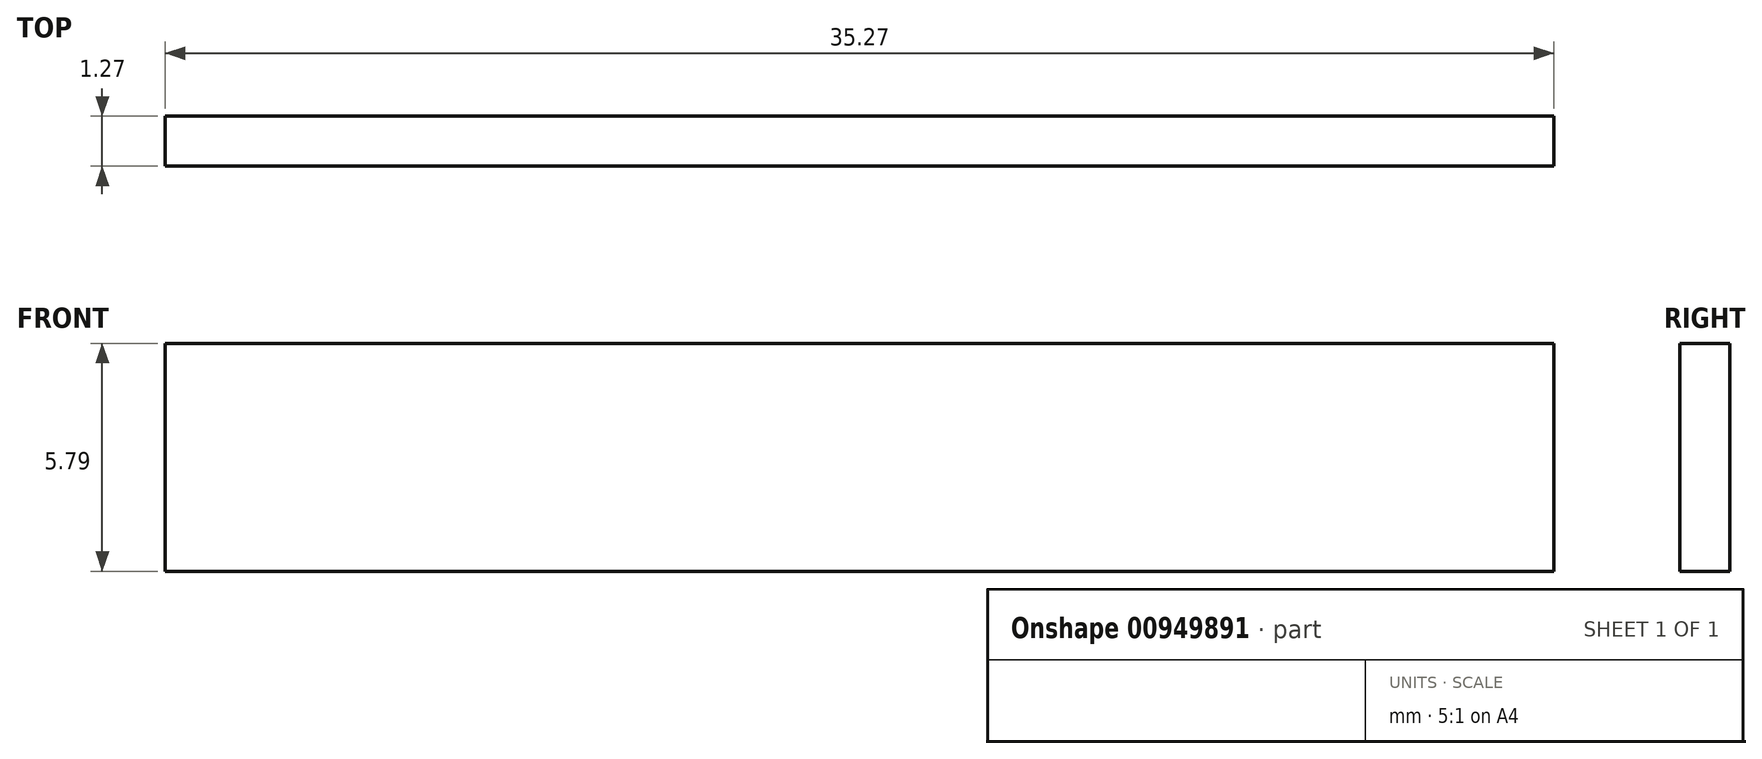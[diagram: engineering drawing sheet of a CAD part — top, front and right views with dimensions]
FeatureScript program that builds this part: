
annotation { "Feature Type Name" : "Feature", "Feature Type Description" : "" }
export const myFeature = defineFeature(function(context is Context, id is Id, definition is map)
    precondition{}
    {
        {
            var Q0;
            Q0=qCreatedBy(makeId("Front.planeOp"),FACE);
            var sketch = newSketch(context, id + "F0", { "sketchPlane" : qUnion([Q0])});
            skPoint(sketch, "E0.0", {"position": v(0, 0) * mm});
            skLineSegment(sketch, "E1.bottom", {"start": v(0, 0) * mm, "end": v(35.27, 0) * mm});
            skLineSegment(sketch, "E1.top", {"start": v(0, 5.8) * mm, "end": v(35.27, 5.8) * mm});
            skLineSegment(sketch, "E1.left", {"start": v(0, 0) * mm, "end": v(0, 5.8) * mm});
            skLineSegment(sketch, "E1.right", {"start": v(35.27, 0) * mm, "end": v(35.27, 5.8) * mm});
            skSolve(sketch);
        }
        {
            var Q0;
            Q0=makeQuery(id+"F0.imprint","IMPRINT",FACE,{"disambiguationData":[TD([[makeQuery(id+"F0.imprint","IMPRINT",EDGE,{"derivedFrom":sQuery(id+"F0.wireOp",EDGE,"E1.bottom")}),1.0]])]});
            extrude(context, id + "F1", {"entities" : qUnion([Q0]), "depth" : 1.27 * mm, "offsetDistance" : 25.4 * mm});
        }
    });
